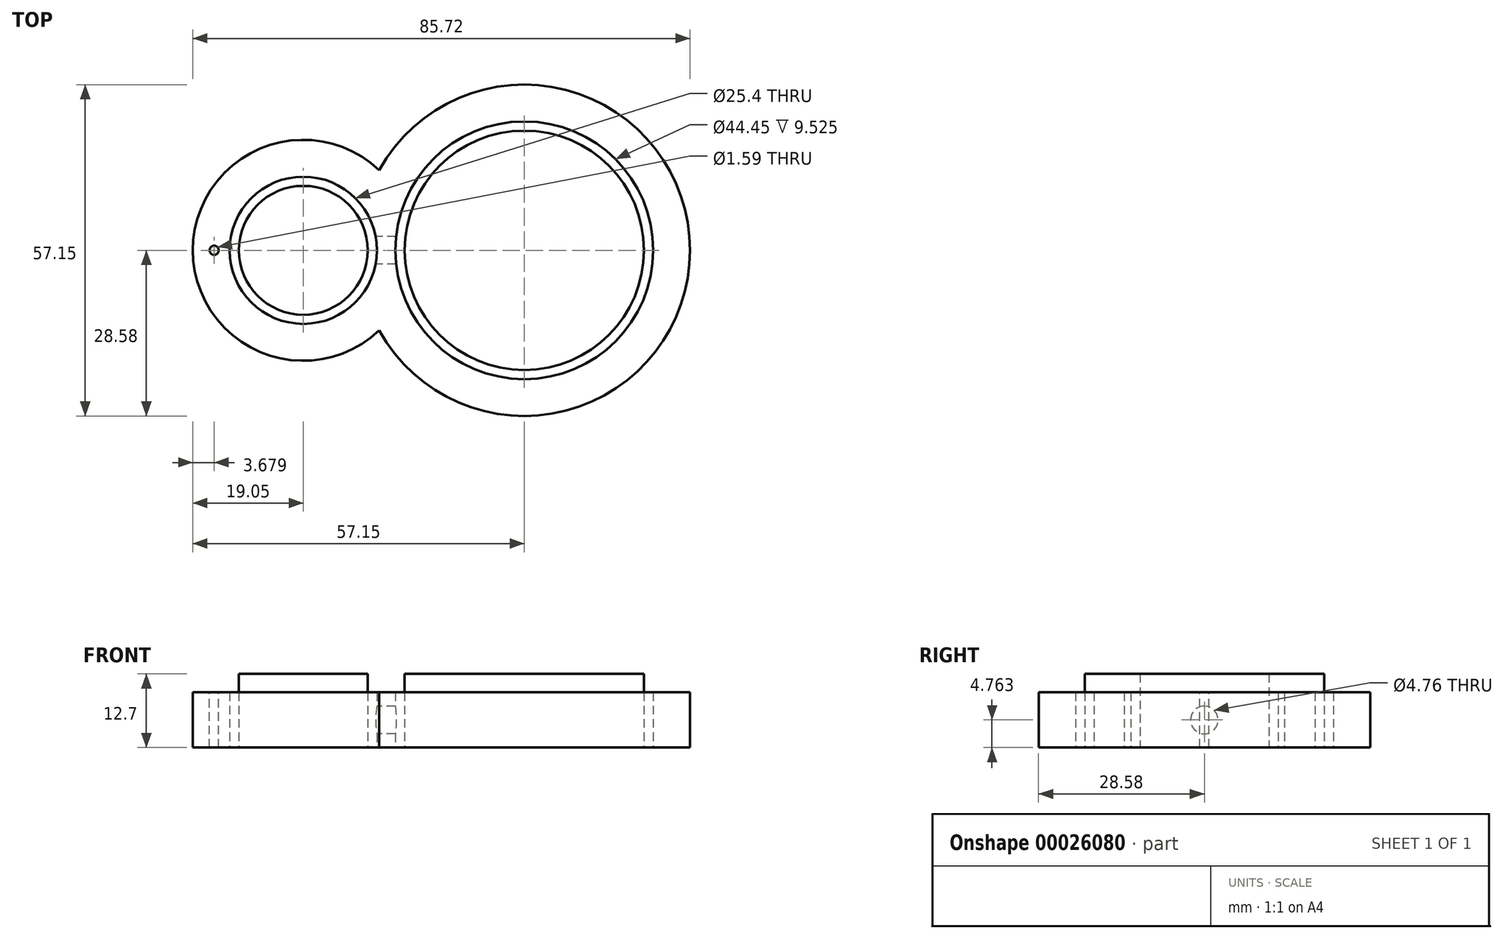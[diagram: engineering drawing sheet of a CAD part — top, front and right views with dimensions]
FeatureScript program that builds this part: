
annotation { "Feature Type Name" : "Feature", "Feature Type Description" : "" }
export const myFeature = defineFeature(function(context is Context, id is Id, definition is map)
    precondition{}
    {
        {
            var Q0;
            Q0=qCreatedBy(makeId("Top.planeOp"),FACE);
            var sketch = newSketch(context, id + "F0", { "sketchPlane" : qUnion([Q0])});
            skCircle(sketch, "E0", {"center": v(0, 0) * mm, "radius": 12.7 * mm});
            skCircle(sketch, "E1", {"center": v(38.1, 0) * mm, "radius": 22.23 * mm});
            skArc(sketch, "E2.0", {"start": v(13.1, 13.83) * mm, "mid": v(-19.05, 0) * mm, "end": v(13.1, -13.83) * mm});
            skArc(sketch, "E3.0", {"start": v(13.1, -13.83) * mm, "mid": v(66.67, 0) * mm, "end": v(13.1, 13.83) * mm});
            skSolve(sketch);
        }
        {
            var Q0;
            Q0=makeQuery(id+"F0.imprint","IMPRINT",FACE,{"disambiguationData":[TD([[makeQuery(id+"F0.imprint","IMPRINT",EDGE,{"derivedFrom":sQuery(id+"F0.wireOp",EDGE,"E0")}),-1.0]])]});
            extrude(context, id + "F1", {"entities" : qUnion([Q0]), "depth" : 9.52 * mm});
        }
        {
            var Q0;
            Q0=qCreatedBy(makeId("Right.planeOp"),FACE);
            var sketch = newSketch(context, id + "F2", { "sketchPlane" : qUnion([Q0])});
            skCircle(sketch, "E4", {"center": v(0, 4.76) * mm, "radius": 2.38 * mm});
            skSolve(sketch);
        }
        {
            var Q0;
            Q0 = qSketchRegion(id + "F2", true);
            var Q1;
            Q1=makeQuery(id+"F1.opExtrude","SWEPT_FACE",FACE,{"disambiguationData":[OSD([sQuery(id+"F0.wireOp",EDGE,"E1")])]});
            extrude(context, id + "F3", {"entities" : qUnion([Q0]), "operationType" : NewBodyOperationType.REMOVE, "endBound" : BoundingType.UP_TO_SURFACE, "endBoundEntityFace" : qUnion([Q1]), "depth" : 25.4 * mm});
        }
        {
            var Q0;
            Q0=makeQuery(id+"F1.opExtrude","CAP_FACE",FACE,{"disambiguationData":[OSD([sQuery(id+"F0.wireOp",EDGE,"E0"),sQuery(id+"F0.wireOp",EDGE,"E1"),sQuery(id+"F0.wireOp",EDGE,"E2.0"),sQuery(id+"F0.wireOp",EDGE,"E3.0")])],"isStart":false});
            var sketch = newSketch(context, id + "F4", { "sketchPlane" : qUnion([Q0])});
            skCircle(sketch, "E5", {"center": v(0.5, 0) * mm, "radius": 15.88 * mm, "construction": true});
            skCircle(sketch, "E6", {"center": v(-15.37, 0) * mm, "radius": 0.8 * mm});
            skSolve(sketch);
        }
        {
            var Q0;
            Q0=makeQuery(id+"F4.imprint","IMPRINT",FACE,{"disambiguationData":[TD([[makeQuery(id+"F4.imprint","IMPRINT",EDGE,{"derivedFrom":sQuery(id+"F4.wireOp",EDGE,"E6")}),1.0]])]});
            extrude(context, id + "F5", {"entities" : qUnion([Q0]), "operationType" : NewBodyOperationType.REMOVE, "endBound" : BoundingType.THROUGH_ALL, "oppositeDirection" : true, "depth" : 25.4 * mm});
        }
        {
            var Q0;
            Q0=qCreatedBy(makeId("Top.planeOp"),FACE);
            var sketch = newSketch(context, id + "F6", { "sketchPlane" : qUnion([Q0])});
            skCircle(sketch, "E7.0", {"center": v(38.1, 0) * mm, "radius": 22.23 * mm, "construction": true});
            skCircle(sketch, "E8.0", {"center": v(0, 0) * mm, "radius": 12.7 * mm, "construction": true});
            skCircle(sketch, "E9", {"center": v(0, 0) * mm, "radius": 11.11 * mm});
            skCircle(sketch, "E10", {"center": v(38.1, 0) * mm, "radius": 20.64 * mm});
            skSolve(sketch);
        }
        {
            var Q0;
            Q0=makeQuery(id+"F6.imprint","IMPRINT",FACE,{"disambiguationData":[TD([[makeQuery(id+"F6.imprint","IMPRINT",EDGE,{"derivedFrom":sQuery(id+"F6.wireOp",EDGE,"E9")}),1.0]])]});
            extrude(context, id + "F7", {"entities" : qUnion([Q0]), "depth" : 12.7 * mm});
        }
        {
            var Q0;
            Q0=makeQuery(id+"F6.imprint","IMPRINT",FACE,{"disambiguationData":[TD([[makeQuery(id+"F6.imprint","IMPRINT",EDGE,{"derivedFrom":sQuery(id+"F6.wireOp",EDGE,"E10")}),1.0]])]});
            extrude(context, id + "F8", {"entities" : qUnion([Q0]), "depth" : 12.7 * mm});
        }
    });
